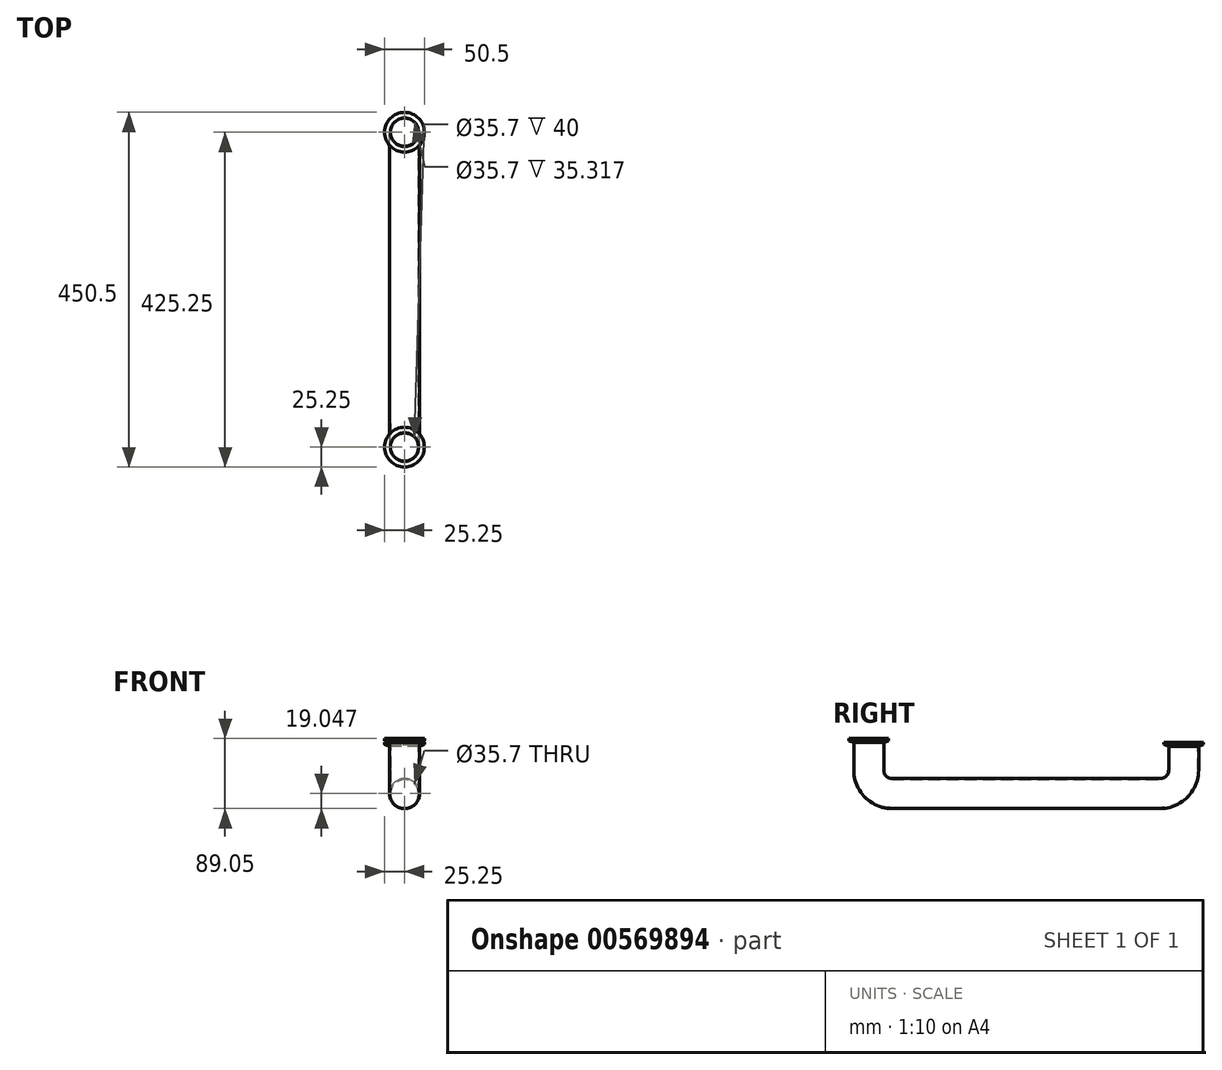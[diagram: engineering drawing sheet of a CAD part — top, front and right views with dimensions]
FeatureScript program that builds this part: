
annotation { "Feature Type Name" : "Feature", "Feature Type Description" : "" }
export const myFeature = defineFeature(function(context is Context, id is Id, definition is map)
    precondition{}
    {
        {
            var Q0;
            Q0=qCreatedBy(makeId("Front.planeOp"),FACE);
            var sketch = newSketch(context, id + "F0", { "sketchPlane" : qUnion([Q0])});
            skLineSegment(sketch, "E0", {"start": v(17.85, 0) * mm, "end": v(17.85, 5.1) * mm});
            skLineSegment(sketch, "E1", {"start": v(17.85, 5.1) * mm, "end": v(25.25, 5.1) * mm});
            skLineSegment(sketch, "E2", {"start": v(25.25, 5.1) * mm, "end": v(25.25, 2.26) * mm});
            skLineSegment(sketch, "E3", {"start": v(25.25, 2.26) * mm, "end": v(19.05, 0) * mm});
            skLineSegment(sketch, "E4", {"start": v(19.05, 0) * mm, "end": v(17.85, 0) * mm});
            skLineSegment(sketch, "E5", {"start": v(0, 0) * mm, "end": v(0, 11.29) * mm, "construction": true});
            skSolve(sketch);
        }
        {
            var Q0;
            Q0=qSketchRegion(id+"F0",true);
            var Q1;
            Q1=sQuery(id+"F0.wireOp",EDGE,"E5");
            revolve(context, id + "F1", {"entities" : qUnion([Q0]), "axis" : qUnion([Q1]), "revolveType" : RevolveType.FULL});
        }
        {
            var Q0;
            Q0=qCreatedBy(makeId("Top.planeOp"),FACE);
            var sketch = newSketch(context, id + "F2", { "sketchPlane" : qUnion([Q0])});
            skCircle(sketch, "E6", {"center": v(0, 0) * mm, "radius": 19.05 * mm});
            skCircle(sketch, "E7", {"center": v(0, 0) * mm, "radius": 17.85 * mm});
            skSolve(sketch);
        }
        {
            var Q0;
            Q0=qCreatedBy(makeId("Right.planeOp"),FACE);
            var sketch = newSketch(context, id + "F3", { "sketchPlane" : qUnion([Q0])});
            skLineSegment(sketch, "E8", {"start": v(0, 0) * mm, "end": v(0, -34.9) * mm});
            skLineSegment(sketch, "E9", {"start": v(30, -64.9) * mm, "end": v(370, -64.9) * mm});
            skPoint(sketch, "E10.visualSharp", {"position": v(0, -64.9) * mm});
            skArc(sketch, "E10.filletArc", {"start": v(0, -34.9) * mm, "mid": v(8.79, -56.1) * mm, "end": v(30, -64.9) * mm});
            skLineSegment(sketch, "E11", {"start": v(400, -34.9) * mm, "end": v(400, -4.68) * mm});
            skPoint(sketch, "E12.visualSharp", {"position": v(400, -64.9) * mm});
            skArc(sketch, "E12.filletArc", {"start": v(370, -64.9) * mm, "mid": v(391.21, -56.1) * mm, "end": v(400, -34.9) * mm});
            skSolve(sketch);
        }
        {
            var Q0;
            Q0=qSketchRegion(id+"F2",true);
            var Q1;
            Q1=qConstructionFilter(qBodyType(qCreatedBy(id+"F3",EDGE),BodyType.WIRE),ConstructionObject.NO);
            sweep(context, id + "F4", {"operationType" : NewBodyOperationType.ADD, "profiles" : qUnion([Q0]), "path" : qUnion([Q1])});
        }
        {
            var Q0;
            Q0=qCreatedBy(makeId("Right.planeOp"),FACE);
            var sketch = newSketch(context, id + "F5", { "sketchPlane" : qUnion([Q0])});
            skLineSegment(sketch, "E13", {"start": v(417.85, -4.68) * mm, "end": v(417.85, 0.42) * mm});
            skLineSegment(sketch, "E14", {"start": v(417.85, 0.42) * mm, "end": v(425.25, 0.42) * mm});
            skLineSegment(sketch, "E15", {"start": v(425.25, 0.42) * mm, "end": v(425.25, -2.43) * mm});
            skLineSegment(sketch, "E16", {"start": v(425.25, -2.43) * mm, "end": v(419.05, -4.68) * mm});
            skLineSegment(sketch, "E17", {"start": v(419.05, -4.68) * mm, "end": v(417.85, -4.68) * mm});
            skSolve(sketch);
        }
        {
            var Q0;
            Q0 = qSketchRegion(id + "F5", true);
            var Q1;
            Q1=sQuery(id+"F3.wireOp",EDGE,"E11");
            revolve(context, id + "F6", {"operationType" : NewBodyOperationType.ADD, "entities" : qUnion([Q0]), "axis" : qUnion([Q1]), "revolveType" : RevolveType.FULL});
        }
    });
